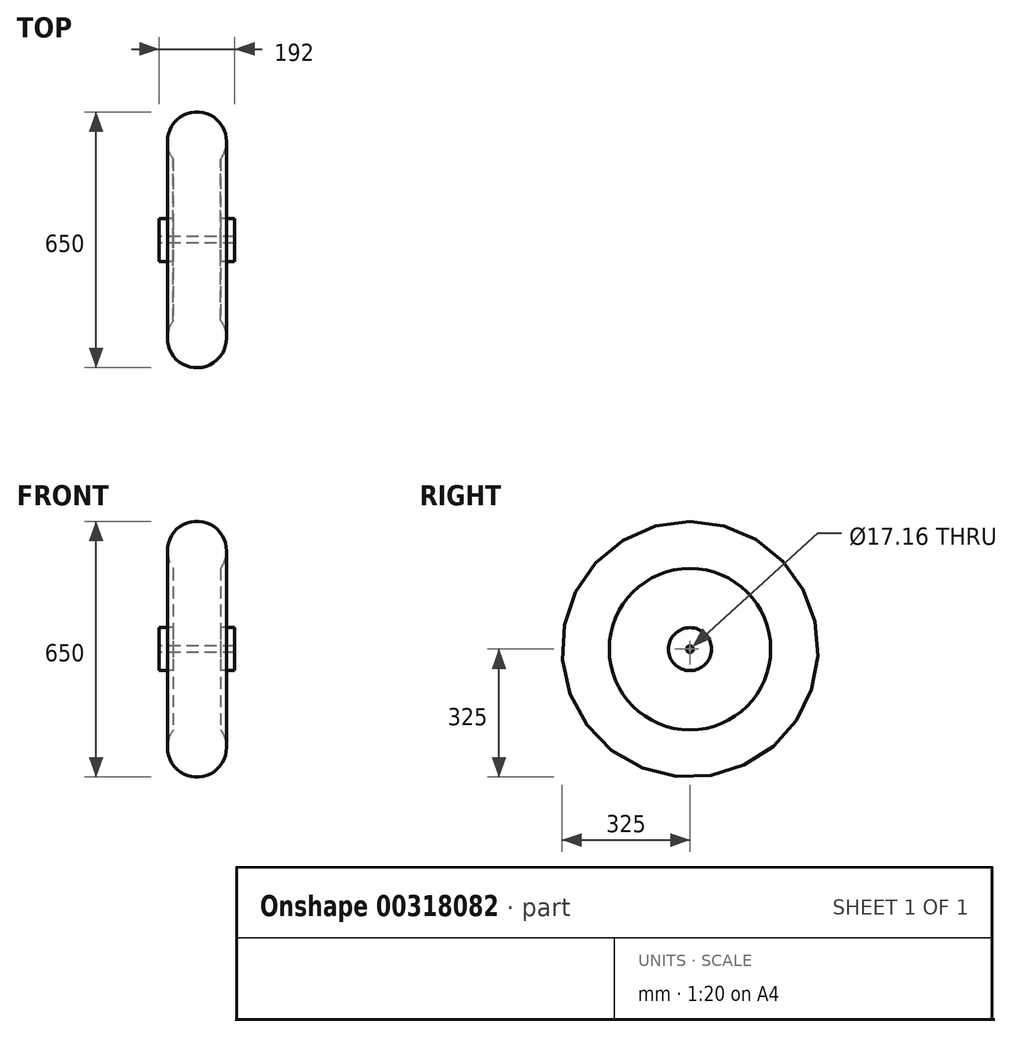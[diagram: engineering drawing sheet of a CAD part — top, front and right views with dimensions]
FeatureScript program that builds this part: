
annotation { "Feature Type Name" : "Feature", "Feature Type Description" : "" }
export const myFeature = defineFeature(function(context is Context, id is Id, definition is map)
    precondition{}
    {
        {
            var Q0;
            Q0=qCreatedBy(makeId("Front.planeOp"),FACE);
            var sketch = newSketch(context, id + "F0", { "sketchPlane" : qUnion([Q0])});
            skPoint(sketch, "E0.third.point", {"position": v(0, 8.58) * mm});
            skLineSegment(sketch, "E1", {"start": v(-96, 8.58) * mm, "end": v(-96, 54.58) * mm});
            skLineSegment(sketch, "E2", {"start": v(-96, 54.58) * mm, "end": v(-60, 54.58) * mm});
            skLineSegment(sketch, "E3", {"start": v(-60, 54.58) * mm, "end": v(-60, 205) * mm});
            skCircle(sketch, "E4", {"center": v(0, 250) * mm, "radius": 75 * mm});
            skLineSegment(sketch, "E5.MirrorCS", {"start": v(60, 54.58) * mm, "end": v(60, 205) * mm});
            skLineSegment(sketch, "E6.MirrorCS", {"start": v(96, 54.58) * mm, "end": v(60, 54.58) * mm});
            skLineSegment(sketch, "E7.MirrorCS", {"start": v(96, 8.58) * mm, "end": v(96, 54.58) * mm});
            skLineSegment(sketch, "E8", {"start": v(-96, 8.58) * mm, "end": v(96, 8.58) * mm});
            skLineSegment(sketch, "E9", {"start": v(-39.46, 0) * mm, "end": v(39.46, 0) * mm, "construction": true});
            skSolve(sketch);
        }
        {
            var Q0;
            Q0=qSketchRegion(id+"F0",true);
            var Q1;
            Q1=sQuery(id+"F0.wireOp",EDGE,"E9");
            revolve(context, id + "F1", {"entities" : qUnion([Q0]), "axis" : qUnion([Q1]), "revolveType" : RevolveType.FULL});
        }
        {
            var Q0;
            Q0=makeQuery(id+"F1.opRevolve","SWEPT_FACE",FACE,{"disambiguationData":[OSD([sQuery(id+"F0.wireOp",EDGE,"E3")])]});
            var sketch = newSketch(context, id + "F2", { "sketchPlane" : qUnion([Q0])});
            skArc(sketch, "E10.0", {"start": v(-45.57, 48.54) * mm, "mid": v(0, -66.58) * mm, "end": v(45.57, 48.54) * mm});
            skArc(sketch, "E11.0", {"start": v(-101.3, 164.27) * mm, "mid": v(0, -193) * mm, "end": v(101.3, 164.27) * mm});
            skCircle(sketch, "E12.0", {"center": v(0, 0) * mm, "radius": 210 * mm});
            skLineSegment(sketch, "E13", {"start": v(0, 66.58) * mm, "end": v(0, 193) * mm, "construction": true});
            skCircle(sketch, "E14.cCircle", {"center": v(0, 0) * mm, "radius": 173.89 * mm, "construction": true});
            skLineSegment(sketch, "E14.0", {"start": v(-83.74, 173.89) * mm, "end": v(83.74, 173.89) * mm, "construction": true});
            skLineSegment(sketch, "E14.1", {"start": v(83.74, 173.89) * mm, "end": v(188.16, 42.95) * mm, "construction": true});
            skLineSegment(sketch, "E14.2", {"start": v(188.16, 42.95) * mm, "end": v(150.9, -120.33) * mm, "construction": true});
            skLineSegment(sketch, "E14.3", {"start": v(150.9, -120.33) * mm, "end": v(0, -193) * mm, "construction": true});
            skLineSegment(sketch, "E14.4", {"start": v(0, -193) * mm, "end": v(-150.9, -120.33) * mm, "construction": true});
            skLineSegment(sketch, "E14.5", {"start": v(-150.9, -120.33) * mm, "end": v(-188.16, 42.95) * mm, "construction": true});
            skLineSegment(sketch, "E14.6", {"start": v(-188.16, 42.95) * mm, "end": v(-83.74, 173.89) * mm, "construction": true});
            skPoint(sketch, "E14.0.midPoint", {"position": v(0, 173.89) * mm});
            skLineSegment(sketch, "E15", {"start": v(-83.74, 173.89) * mm, "end": v(-28.89, 59.99) * mm, "construction": true});
            skLineSegment(sketch, "E16", {"start": v(83.74, 173.89) * mm, "end": v(28.89, 59.99) * mm, "construction": true});
            skLineSegment(sketch, "E17", {"start": v(-60.3, 171.32) * mm, "end": v(-12.55, 72.16) * mm});
            skLineSegment(sketch, "E18", {"start": v(-101.3, 164.27) * mm, "end": v(-45.57, 48.54) * mm});
            skLineSegment(sketch, "E19.MirrorCS", {"start": v(101.3, 164.27) * mm, "end": v(45.57, 48.54) * mm});
            skLineSegment(sketch, "E20.MirrorCS", {"start": v(60.3, 171.32) * mm, "end": v(12.55, 72.16) * mm});
            skLineSegment(sketch, "E21", {"start": v(65.16, 13.7) * mm, "end": v(229, -8.28) * mm, "construction": true});
            skPoint(sketch, "E22.visualSharp", {"position": v(-65.27, 181.63) * mm});
            skArc(sketch, "E22.filletArc", {"start": v(-54.1, 185.26) * mm, "mid": v(-60.43, 179.73) * mm, "end": v(-60.3, 171.32) * mm});
            skArc(sketch, "E23.trimOffspring", {"start": v(54.1, 185.26) * mm, "mid": v(0, 193) * mm, "end": v(-54.1, 185.26) * mm});
            skPoint(sketch, "E24.visualSharp", {"position": v(65.27, 181.63) * mm});
            skArc(sketch, "E24.filletArc", {"start": v(60.3, 171.32) * mm, "mid": v(60.43, 179.73) * mm, "end": v(54.1, 185.26) * mm});
            skArc(sketch, "E25.trimOffspring", {"start": v(3.08, 66.5) * mm, "mid": v(0, 66.58) * mm, "end": v(-3.08, 66.5) * mm});
            skPoint(sketch, "E26.visualSharp", {"position": v(9.53, 65.9) * mm});
            skArc(sketch, "E26.filletArc", {"start": v(3.08, 66.5) * mm, "mid": v(8.67, 67.91) * mm, "end": v(12.55, 72.16) * mm});
            skPoint(sketch, "E27.visualSharp", {"position": v(-9.53, 65.9) * mm});
            skArc(sketch, "E27.filletArc", {"start": v(-12.55, 72.16) * mm, "mid": v(-8.67, 67.91) * mm, "end": v(-3.08, 66.5) * mm});
            skSolve(sketch);
        }
        {
            var Q0;
            Q0=makeQuery(id+"F2.imprint","IMPRINT",FACE,{"disambiguationData":[TD([[makeQuery(id+"F2.imprint","IMPRINT",EDGE,{"derivedFrom":sQuery(id+"F2.wireOp",EDGE,"E17")}),1.0]])]});
            extrude(context, id + "F3", {"entities" : qUnion([Q0]), "operationType" : NewBodyOperationType.ADD, "oppositeDirection" : true, "depth" : 25 * mm});
        }
    });
